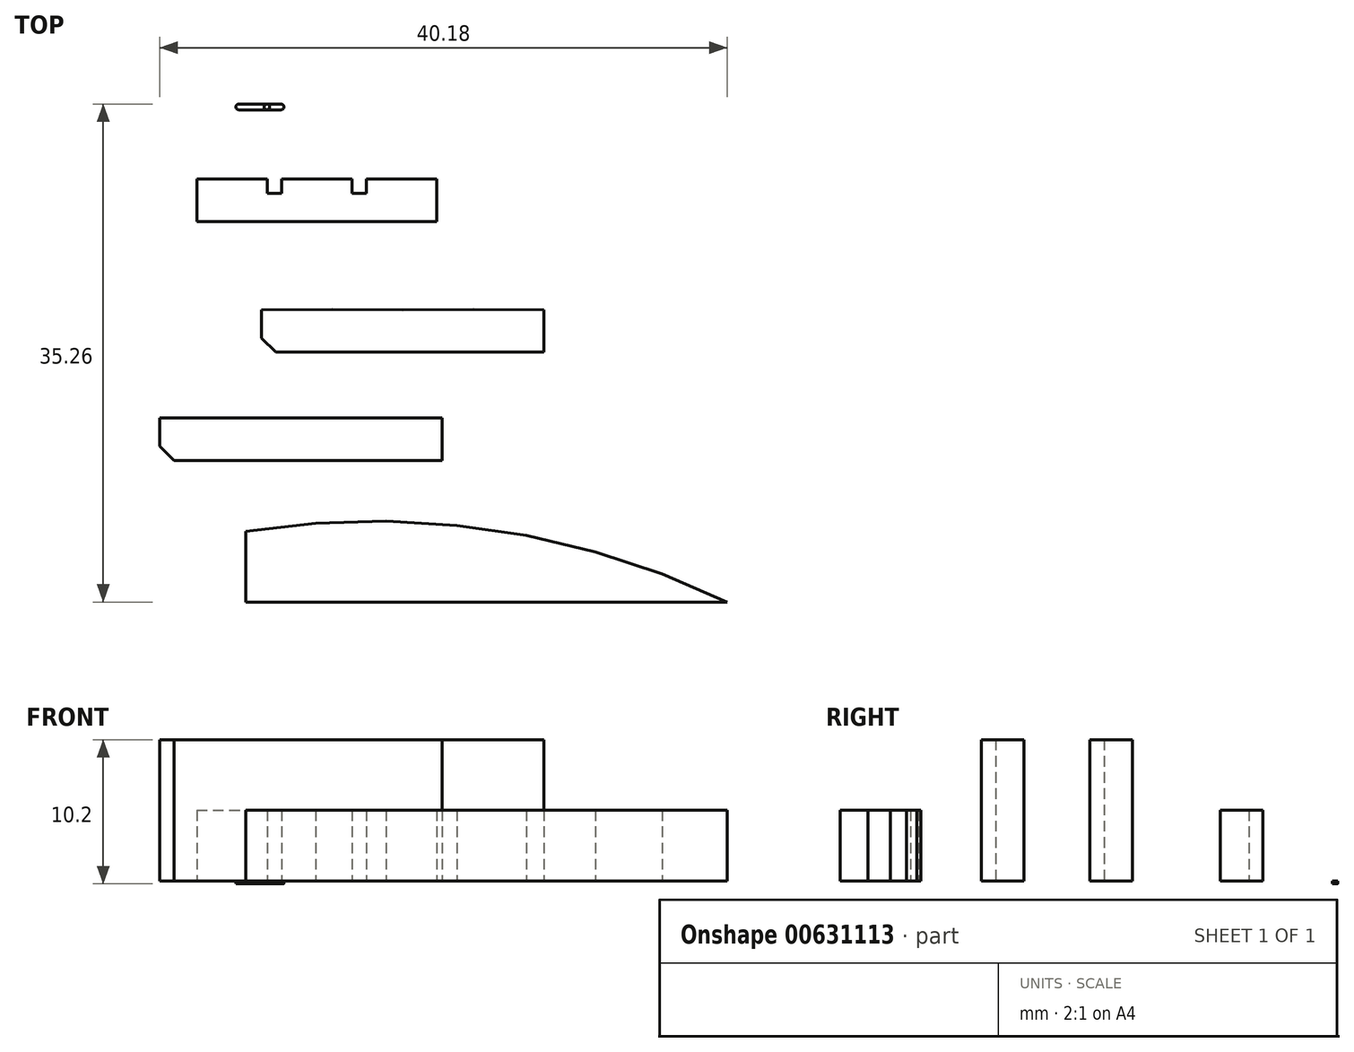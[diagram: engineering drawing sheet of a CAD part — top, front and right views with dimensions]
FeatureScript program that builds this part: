
annotation { "Feature Type Name" : "Feature", "Feature Type Description" : "" }
export const myFeature = defineFeature(function(context is Context, id is Id, definition is map)
    precondition{}
    {
        {
            var Q0;
            Q0=qCreatedBy(makeId("Top.planeOp"),FACE);
            var sketch = newSketch(context, id + "F0", { "sketchPlane" : qUnion([Q0])});
            skCircle(sketch, "E0", {"center": v(-63.7, 42.2) * mm, "radius": 0.2 * mm});
            skCircle(sketch, "E1", {"center": v(-61.7, 42.2) * mm, "radius": 0.2 * mm});
            skLineSegment(sketch, "E2", {"start": v(-63.7, 42.2) * mm, "end": v(-61.7, 42.2) * mm, "construction": true});
            skLineSegment(sketch, "E3", {"start": v(-61.7, 42.4) * mm, "end": v(-63.7, 42.4) * mm});
            skLineSegment(sketch, "E4", {"start": v(-61.7, 42) * mm, "end": v(-63.7, 42) * mm});
            skSolve(sketch);
        }
        {
            var Q0;
            Q0 = qSketchRegion(id + "F0", true);
            extrude(context, id + "F1", {"entities" : qUnion([Q0]), "oppositeDirection" : true, "depth" : 0.2 * mm, "offsetDistance" : 25 * mm});
        }
        {
            var Q0;
            Q0=qCreatedBy(makeId("Top.planeOp"),FACE);
            var sketch = newSketch(context, id + "F2", { "sketchPlane" : qUnion([Q0])});
            skCircle(sketch, "E5", {"center": v(-60.7, 42.2) * mm, "radius": 0.2 * mm});
            skCircle(sketch, "E6", {"center": v(-61.7, 42.2) * mm, "radius": 0.2 * mm});
            skLineSegment(sketch, "E7", {"start": v(-60.7, 42.2) * mm, "end": v(-61.7, 42.2) * mm, "construction": true});
            skLineSegment(sketch, "E8", {"start": v(-61.7, 42) * mm, "end": v(-60.7, 42) * mm});
            skLineSegment(sketch, "E9", {"start": v(-61.7, 42.4) * mm, "end": v(-60.7, 42.4) * mm});
            skSolve(sketch);
        }
        {
            var Q0;
            Q0 = qSketchRegion(id + "F2", true);
            extrude(context, id + "F3", {"entities" : qUnion([Q0]), "oppositeDirection" : true, "depth" : 0.2 * mm, "offsetDistance" : 25 * mm});
        }
        {
            var Q0;
            Q0=qCreatedBy(makeId("Top.planeOp"),FACE);
            var sketch = newSketch(context, id + "F4", { "sketchPlane" : qUnion([Q0])});
            skLineSegment(sketch, "E10.bottom", {"start": v(-66.67, 37.08) * mm, "end": v(-61.67, 37.08) * mm});
            skLineSegment(sketch, "E10.top", {"start": v(-66.67, 34.08) * mm, "end": v(-49.67, 34.08) * mm});
            skLineSegment(sketch, "E10.left", {"start": v(-66.67, 37.08) * mm, "end": v(-66.67, 34.08) * mm});
            skLineSegment(sketch, "E11.bottom", {"start": v(-61.67, 36.08) * mm, "end": v(-60.67, 36.08) * mm});
            skLineSegment(sketch, "E12.bottom", {"start": v(-60.67, 37.08) * mm, "end": v(-55.67, 37.08) * mm});
            skLineSegment(sketch, "E12.right", {"start": v(-55.67, 37.08) * mm, "end": v(-55.67, 36.08) * mm});
            skLineSegment(sketch, "E13.bottom", {"start": v(-55.67, 36.08) * mm, "end": v(-54.67, 36.08) * mm});
            skLineSegment(sketch, "E14.bottom", {"start": v(-54.67, 37.08) * mm, "end": v(-49.67, 37.08) * mm});
            skLineSegment(sketch, "E14.left", {"start": v(-54.67, 37.08) * mm, "end": v(-54.67, 36.08) * mm});
            skLineSegment(sketch, "E15.left", {"start": v(-49.67, 37.08) * mm, "end": v(-49.67, 34.08) * mm});
            skLineSegment(sketch, "E16", {"start": v(-61.67, 37.08) * mm, "end": v(-61.67, 36.08) * mm});
            skLineSegment(sketch, "E17", {"start": v(-60.67, 36.08) * mm, "end": v(-60.67, 37.08) * mm});
            skSolve(sketch);
        }
        {
            var Q0;
            Q0=makeQuery(id+"F4.imprint","IMPRINT",FACE,{"disambiguationData":[TD([[makeQuery(id+"F4.imprint","IMPRINT",EDGE,{"derivedFrom":sQuery(id+"F4.wireOp",EDGE,"E10.bottom")}),-1.0]])]});
            extrude(context, id + "F5", {"entities" : qUnion([Q0]), "depth" : 5 * mm, "offsetDistance" : 25 * mm});
        }
        {
            var Q0;
            Q0=qCreatedBy(makeId("Top.planeOp"),FACE);
            var sketch = newSketch(context, id + "F6", { "sketchPlane" : qUnion([Q0])});
            skLineSegment(sketch, "E18.bottom", {"start": v(-62.08, 27.83) * mm, "end": v(-57.08, 27.85) * mm});
            skLineSegment(sketch, "E18.left", {"start": v(-62.08, 27.83) * mm, "end": v(-62.08, 25.83) * mm});
            skLineSegment(sketch, "E19.bottom", {"start": v(-57.08, 27.85) * mm, "end": v(-52.08, 27.83) * mm});
            skLineSegment(sketch, "E20.bottom", {"start": v(-52.08, 27.83) * mm, "end": v(-47.08, 27.85) * mm});
            skLineSegment(sketch, "E21.bottom", {"start": v(-47.08, 27.85) * mm, "end": v(-42.08, 27.83) * mm});
            skLineSegment(sketch, "E22", {"start": v(-42.08, 27.83) * mm, "end": v(-42.08, 24.83) * mm});
            skLineSegment(sketch, "E23", {"start": v(-61.08, 24.83) * mm, "end": v(-42.08, 24.83) * mm});
            skLineSegment(sketch, "E24", {"start": v(-52.08, 27.83) * mm, "end": v(-52.08, 24.83) * mm, "construction": true});
            skLineSegment(sketch, "E25", {"start": v(-62.08, 25.83) * mm, "end": v(-61.08, 24.83) * mm});
            skPoint(sketch, "E26.orphan", {"position": v(-62.08, 24.83) * mm});
            skSolve(sketch);
        }
        {
            var Q0;
            Q0=makeQuery(id+"F6.imprint","IMPRINT",FACE,{"disambiguationData":[TD([[makeQuery(id+"F6.imprint","IMPRINT",EDGE,{"derivedFrom":sQuery(id+"F6.wireOp",EDGE,"E18.bottom")}),-1.0]])]});
            var Q1;
            {var subQ0=sQuery(id+"F6.wireOp",EDGE,"d7muVBTr-JA5V-jX8C-5ovv-0FzP7LmB190D");Q1=makeQuery(id+"F6.imprint","IMPRINT",FACE,{"disambiguationData":[TD([[makeQuery(id+"F6.imprint","IMPRINT",EDGE,{"derivedFrom":subQ0}),1.0]])]});}
            var Q2;
            Q2=makeQuery(id+"F6.imprint","IMPRINT",FACE,{"disambiguationData":[TD([[makeQuery(id+"F6.imprint","IMPRINT",EDGE,{"derivedFrom":sQuery(id+"F6.wireOp",EDGE,"E20.bottom")}),-1.0]])]});
            var Q3;
            {var subQ0=sQuery(id+"F6.wireOp",EDGE,"0f625a3b-a311-432e-9dd9-493c1f0f0de9");Q3=makeQuery(id+"F6.imprint","IMPRINT",FACE,{"disambiguationData":[TD([[makeQuery(id+"F6.imprint","IMPRINT",EDGE,{"derivedFrom":subQ0}),1.0]])]});}
            extrude(context, id + "F7", {"entities" : qUnion([Q0, Q1, Q2, Q3]), "depth" : 10 * mm, "offsetDistance" : 25 * mm});
        }
        {
            var Q0;
            Q0=qCreatedBy(makeId("Top.planeOp"),FACE);
            var sketch = newSketch(context, id + "F8", { "sketchPlane" : qUnion([Q0])});
            skLineSegment(sketch, "E27.bottom", {"start": v(-69.29, 20.15) * mm, "end": v(-64.29, 20.16) * mm});
            skLineSegment(sketch, "E27.left", {"start": v(-69.29, 20.15) * mm, "end": v(-69.29, 18.15) * mm});
            skLineSegment(sketch, "E28.bottom", {"start": v(-64.29, 20.16) * mm, "end": v(-59.29, 20.15) * mm});
            skLineSegment(sketch, "E29.bottom", {"start": v(-59.29, 20.15) * mm, "end": v(-54.29, 20.16) * mm});
            skLineSegment(sketch, "E30.bottom", {"start": v(-54.29, 20.16) * mm, "end": v(-49.29, 20.15) * mm});
            skLineSegment(sketch, "E31", {"start": v(-49.29, 20.15) * mm, "end": v(-49.29, 17.15) * mm});
            skLineSegment(sketch, "E32", {"start": v(-68.29, 17.15) * mm, "end": v(-49.29, 17.15) * mm});
            skLineSegment(sketch, "E33", {"start": v(-59.29, 20.15) * mm, "end": v(-59.29, 17.15) * mm, "construction": true});
            skLineSegment(sketch, "E34", {"start": v(-69.29, 18.15) * mm, "end": v(-68.29, 17.15) * mm});
            skPoint(sketch, "E35.orphan", {"position": v(-69.29, 17.15) * mm});
            skSolve(sketch);
        }
        {
            var Q0;
            Q0 = qSketchRegion(id + "F8", true);
            extrude(context, id + "F9", {"entities" : qUnion([Q0]), "depth" : 10 * mm, "offsetDistance" : 25 * mm});
        }
        {
            var Q0;
            Q0=qCreatedBy(makeId("Top.planeOp"),FACE);
            var sketch = newSketch(context, id + "F10", { "sketchPlane" : qUnion([Q0])});
            skLineSegment(sketch, "E36", {"start": v(-29.1, 7.13) * mm, "end": v(-63.21, 7.13) * mm});
            skLineSegment(sketch, "E37", {"start": v(-63.21, 7.13) * mm, "end": v(-63.21, 12.13) * mm});
            skLineSegment(sketch, "E38", {"start": v(-63.21, 12.13) * mm, "end": v(-58.25, 12.7) * mm});
            skLineSegment(sketch, "E39", {"start": v(-58.25, 12.7) * mm, "end": v(-53.25, 12.85) * mm});
            skLineSegment(sketch, "E40", {"start": v(-48.26, 12.56) * mm, "end": v(-53.25, 12.85) * mm});
            skLineSegment(sketch, "E41", {"start": v(-48.26, 12.56) * mm, "end": v(-43.31, 11.83) * mm});
            skLineSegment(sketch, "E42", {"start": v(-43.31, 11.83) * mm, "end": v(-38.45, 10.68) * mm});
            skLineSegment(sketch, "E43", {"start": v(-38.45, 10.68) * mm, "end": v(-33.7, 9.1) * mm});
            skLineSegment(sketch, "E44", {"start": v(-33.7, 9.1) * mm, "end": v(-29.1, 7.13) * mm});
            skSolve(sketch);
        }
        {
            var Q0;
            Q0=makeQuery(id+"F10.imprint","IMPRINT",FACE,{"disambiguationData":[TD([[makeQuery(id+"F10.imprint","IMPRINT",EDGE,{"derivedFrom":sQuery(id+"F10.wireOp",EDGE,"E36")}),-1.0]])]});
            extrude(context, id + "F11", {"entities" : qUnion([Q0]), "depth" : 5 * mm, "offsetDistance" : 25 * mm});
        }
    });
